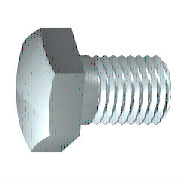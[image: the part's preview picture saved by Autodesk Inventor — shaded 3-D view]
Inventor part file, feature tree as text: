
AUTODESK INVENTOR PART (.ipt)
format: ipt  version: 2021 (Build 250183000, 183)  size: 192,512 bytes
history: native  units: mm (DEFAULTED — no unit token found)
features: sketch x3, extrude x1, chamfer x1, plane x1
ambient origin geometry x7: Origin, YZ Plane, XZ Plane, X Axis, Y Axis, Z Axis, Center Point
bodies: Solid1 (feature_tree), Body (feature_tree)
feature tree (6):
  extrude  "Head"  Depth=46.0mm
  chamfer  "Chamfer1"  Distance=11.7mm
  plane  "Work Plane1"
  sketch  "Sketch1"  dims[d0=95.0mm d1=46.0mm]
  sketch  "Sketch2"  dims[d2=20.0mm]
  sketch  "Sketch4"  dims[d12=90.0deg d3=11.7mm d4=0.0mm d5=30.0deg d21=90.0deg d6=1.533625mm d7=1.533725mm d8=0.0mm d9=0.8001mm d10=28.2mm d11=30.0mm d13=1.533725mm d14=20.0mm d15=46.0mm d16=0.0mm d19=30.0mm d55=45.0deg d57=0.0mm d58=0.0mm]
